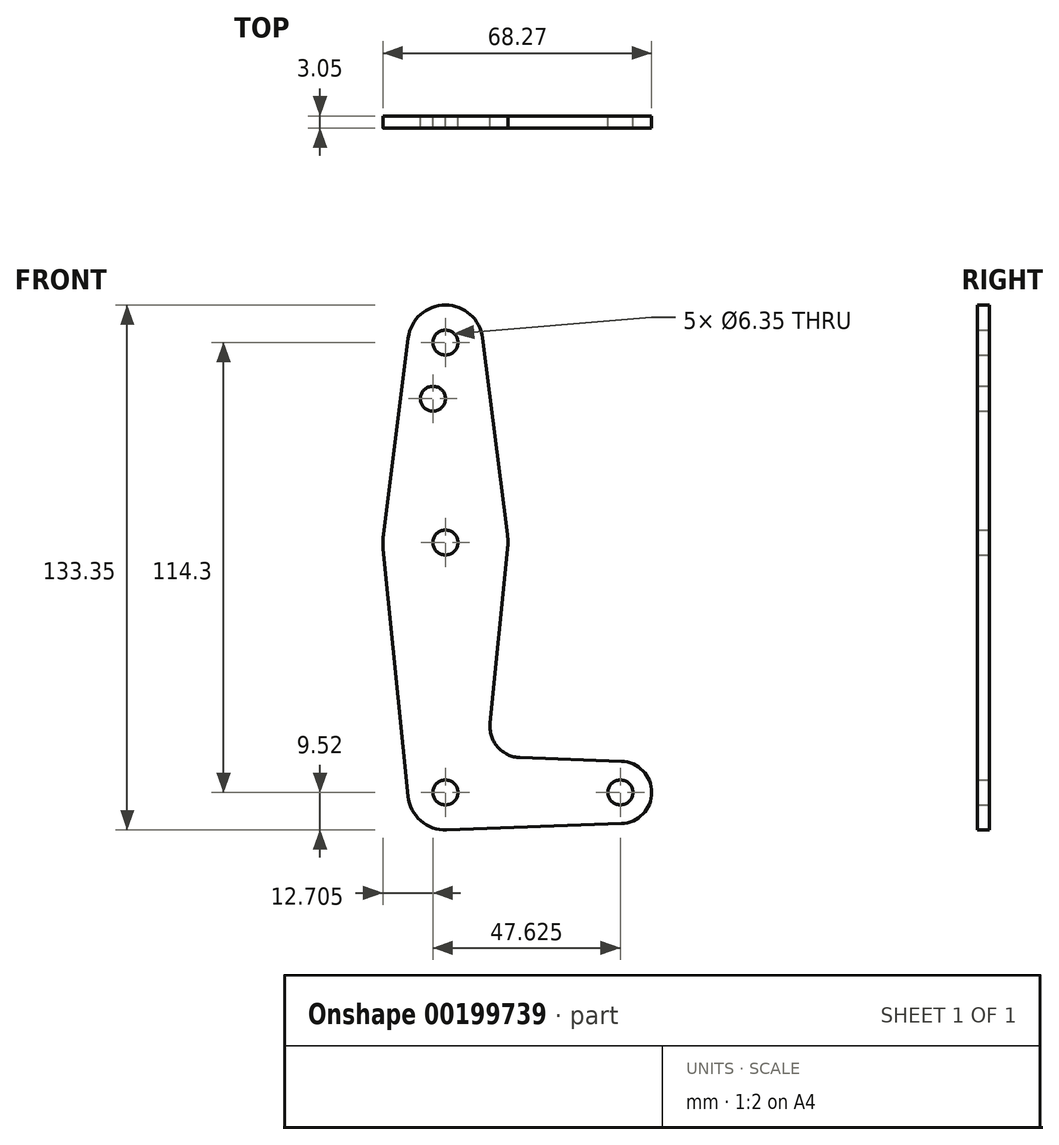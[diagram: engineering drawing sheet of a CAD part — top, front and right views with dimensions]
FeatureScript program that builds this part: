
annotation { "Feature Type Name" : "Feature", "Feature Type Description" : "" }
export const myFeature = defineFeature(function(context is Context, id is Id, definition is map)
    precondition{}
    {
        {
            var Q0;
            Q0=qCreatedBy(makeId("Front.planeOp"),FACE);
            var sketch = newSketch(context, id + "F0", { "sketchPlane" : qUnion([Q0])});
            skLineSegment(sketch, "E0", {"start": v(0, 114.3) * mm, "end": v(0, 0) * mm, "construction": true});
            skLineSegment(sketch, "E1", {"start": v(0, 0) * mm, "end": v(44.45, 0) * mm, "construction": true});
            skCircle(sketch, "E2", {"center": v(0, 114.3) * mm, "radius": 9.53 * mm});
            skCircle(sketch, "E3", {"center": v(0, 63.5) * mm, "radius": 15.88 * mm});
            skCircle(sketch, "E4", {"center": v(0, 0) * mm, "radius": 9.53 * mm});
            skCircle(sketch, "E5", {"center": v(44.45, 0) * mm, "radius": 7.94 * mm});
            skLineSegment(sketch, "E6", {"start": v(-9.45, 115.5) * mm, "end": v(-15.75, 65.48) * mm});
            skLineSegment(sketch, "E7", {"start": v(9.45, 115.5) * mm, "end": v(15.75, 65.48) * mm});
            skLineSegment(sketch, "E8", {"start": v(18.97, 8.85) * mm, "end": v(44.73, 7.93) * mm});
            skLineSegment(sketch, "E9", {"start": v(44.73, -7.93) * mm, "end": v(0.34, -9.52) * mm});
            skLineSegment(sketch, "E10", {"start": v(-15.8, 61.91) * mm, "end": v(-9.48, -0.95) * mm});
            skLineSegment(sketch, "E11", {"start": v(15.8, 61.91) * mm, "end": v(11.34, 17.6) * mm});
            skCircle(sketch, "E12", {"center": v(0, 114.3) * mm, "radius": 3.18 * mm});
            skCircle(sketch, "E13", {"center": v(0, 63.5) * mm, "radius": 3.18 * mm});
            skCircle(sketch, "E14", {"center": v(0, 0) * mm, "radius": 3.18 * mm});
            skCircle(sketch, "E15", {"center": v(44.45, 0) * mm, "radius": 3.18 * mm});
            skCircle(sketch, "E16", {"center": v(-3.17, 100.03) * mm, "radius": 3.18 * mm});
            skArc(sketch, "E17.filletArc", {"start": v(11.34, 17.6) * mm, "mid": v(13.26, 11.57) * mm, "end": v(18.97, 8.85) * mm});
            skSolve(sketch);
        }
        {
            var Q0;
            Q0 = qSketchRegion(id + "F0", true);
            extrude(context, id + "F1", {"entities" : qUnion([Q0]), "depth" : 3.05 * mm});
        }
    });
